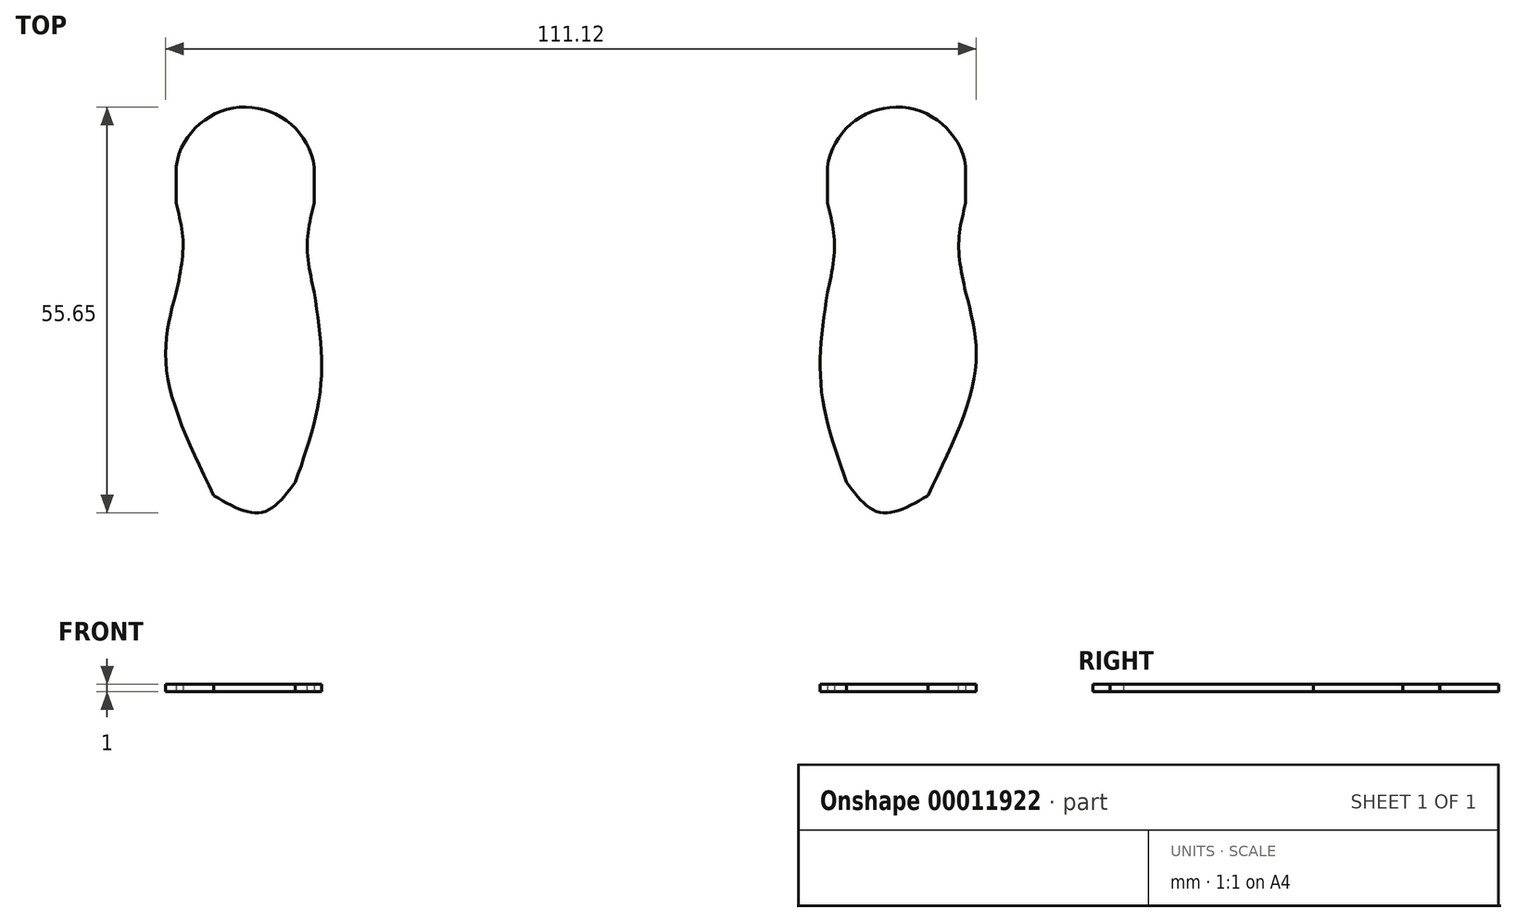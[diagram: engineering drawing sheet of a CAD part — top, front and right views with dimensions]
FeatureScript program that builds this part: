
annotation { "Feature Type Name" : "Feature", "Feature Type Description" : "" }
export const myFeature = defineFeature(function(context is Context, id is Id, definition is map)
    precondition{}
    {
        {
            var Q0;
            Q0=qCreatedBy(makeId("Top.planeOp"),FACE);
            var sketch = newSketch(context, id + "F0", { "sketchPlane" : qUnion([Q0])});
            skArc(sketch, "E0", {"start": v(-35.17, 32) * mm, "mid": v(-44.58, 40.25) * mm, "end": v(-54.12, 32.14) * mm});
            skLineSegment(sketch, "E1", {"start": v(-54.12, 32.14) * mm, "end": v(-54.12, 27.07) * mm});
            skLineSegment(sketch, "E2", {"start": v(-35.17, 32) * mm, "end": v(-35.17, 27.07) * mm});
            skFitSpline(sketch, "E3", {"points": [v(-54.12, 27.07) * mm, v(-53.16, 21.43) * mm, v(-54.12, 14.82) * mm], "startDerivative": vector(2.92, -11.49) * mm, "endDerivative": vector(-2.85, -12.99) * mm});
            skFitSpline(sketch, "E4", {"points": [v(-35.17, 27.07) * mm, v(-36.14, 21.43) * mm, v(-35.17, 14.82) * mm], "startDerivative": vector(-2.97, -11.49) * mm, "endDerivative": vector(2.9, -12.99) * mm});
            skFitSpline(sketch, "E5", {"points": [v(-54.12, 14.82) * mm, v(-55.44, 4.2) * mm, v(-48.93, -13.04) * mm], "startDerivative": vector(-6.18, -23.3) * mm, "endDerivative": vector(15.58, -32.02) * mm});
            skFitSpline(sketch, "E6", {"points": [v(-35.17, 14.82) * mm, v(-34.3, 1.92) * mm, v(-37.77, -11.2) * mm], "startDerivative": vector(3.88, -26.16) * mm, "endDerivative": vector(-9.03, -25.87) * mm});
            skFitSpline(sketch, "E7", {"points": [v(-37.77, -11.2) * mm, v(-42.43, -15.33) * mm, v(-48.93, -13.04) * mm], "startDerivative": vector(-8.8, -11.66) * mm, "endDerivative": vector(-13.49, 7.8) * mm});
            skFitSpline(sketch, "E8.0.MirrorCS", {"points": [v(35.17, 27.07) * mm, v(36.14, 21.43) * mm, v(35.17, 14.82) * mm], "startDerivative": vector(2.97, -11.49) * mm, "endDerivative": vector(-2.9, -12.99) * mm});
            skFitSpline(sketch, "E8.1.MirrorCS", {"points": [v(54.12, 27.07) * mm, v(53.16, 21.43) * mm, v(54.12, 14.82) * mm], "startDerivative": vector(-2.92, -11.49) * mm, "endDerivative": vector(2.85, -12.99) * mm});
            skFitSpline(sketch, "E8.2.MirrorCS", {"points": [v(37.77, -11.2) * mm, v(42.43, -15.33) * mm, v(48.93, -13.04) * mm], "startDerivative": vector(8.8, -11.66) * mm, "endDerivative": vector(13.49, 7.8) * mm});
            skArc(sketch, "E8.3.MirrorCS", {"start": v(35.17, 32) * mm, "mid": v(44.58, 40.25) * mm, "end": v(54.12, 32.14) * mm});
            skFitSpline(sketch, "E8.4.MirrorCS", {"points": [v(35.17, 14.82) * mm, v(34.3, 1.92) * mm, v(37.77, -11.2) * mm], "startDerivative": vector(-3.88, -26.16) * mm, "endDerivative": vector(9.03, -25.87) * mm});
            skLineSegment(sketch, "E8.5.MirrorCS", {"start": v(35.17, 32) * mm, "end": v(35.17, 27.07) * mm});
            skFitSpline(sketch, "E8.6.MirrorCS", {"points": [v(54.12, 14.82) * mm, v(55.44, 4.2) * mm, v(48.93, -13.04) * mm], "startDerivative": vector(6.18, -23.3) * mm, "endDerivative": vector(-15.58, -32.02) * mm});
            skLineSegment(sketch, "E8.7.MirrorCS", {"start": v(54.12, 32.14) * mm, "end": v(54.12, 27.07) * mm});
            skSolve(sketch);
        }
        {
            var Q0;
            Q0=makeQuery(id+"F0.imprint","IMPRINT",FACE,{"disambiguationData":[TD([[makeQuery(id+"F0.imprint","IMPRINT",EDGE,{"derivedFrom":sQuery(id+"F0.wireOp",EDGE,"E0")}),1.0]])]});
            var Q1;
            Q1=makeQuery(id+"F0.imprint","IMPRINT",FACE,{"disambiguationData":[TD([[makeQuery(id+"F0.imprint","IMPRINT",EDGE,{"derivedFrom":sQuery(id+"F0.wireOp",EDGE,"E8.0.MirrorCS")}),1.0]])]});
            extrude(context, id + "F1", {"entities" : qUnion([Q0, Q1]), "depth" : 1 * mm});
        }
    });
